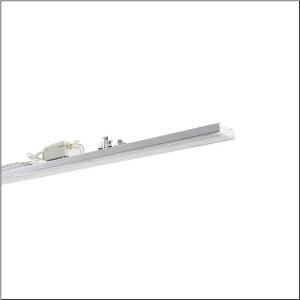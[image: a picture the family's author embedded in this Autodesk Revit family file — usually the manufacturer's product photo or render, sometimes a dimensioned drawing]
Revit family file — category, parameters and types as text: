
# Revit family: licross_r__21_recessed_mo_52tl12dn465g_46f0
name_source: partatom
category: Lighting Fixtures
units: mm (PartAtom-declared; Revit-internal decimal feet)

## family parameters
Cut with Voids When Loaded = No
Host = Face
Light Source = No
Part Type = Normal
Room Calculation Point = No
Round Connector Dimension = Use Diameter
Shared = No

## types (1)
- --- (1 x LED, 6500 lm, 35.1 W, 4000K)
    Apparent Load = 35 VA
    CIE Flux Codes = 72 92 99 100 100
    Color Rendering = 80
    Color Temperature = 4000K
    Default Elevation = 1800 mm
    Description = Licross® 21 Recessed MO, luminaire insert, of sheet steel, galvanised, coil coated, white, length: 1.500mm, width: 66mm, height: 67mm, LED rated luminous flux: 6.500lm, light colour: 840, control gear: DALI 2, with plug, 5-pole, with phase selection, mains connection: 220..240V, AC, 50/60Hz, rated input power: 35W, halogen-free wiring, primary optical cover: cover, of PMMA, light emission: direct distribution, primary light characteristic: symmetric, protection rating (complete): IP40, insulation class (complete): insulation class I (protective earthing), certification: CE, ENEC, VDE, UKCA, protection symbol: D if used in an environment without relevant dust loads with corresponding accessories, impact resistance: IK06, permissible ambient temperature for indoor applications: -25..+45°C, corresponds to IFS (International Featured Standards) requirements for safety and quality in the food industry, reducing of maximum allowable ambient temperature of 5°C with ceiling mounting, LABS conformity tested according to VDMA 24364:2018-05, packaging unit: 1 piece
    Height = 58 mm
    Lamp = 1 x LED
    Lamp Light Flux = 6500 lm
    Lamp Power = 35.1 W
    Lamp count = 1
    Length = 1500 mm
    Luminous efficacy = 185 lm/W
    Manufacturer = Siteco
    ModVariant = No
    Model = 52TL12DN465G
    Mounting Place = Ceiling
    Mounting Type = Pendant
    Number of Poles = 1
    OnlyDefault = Yes
    Power Factor = 1
    Product Name = Licross® 21 Recessed MO
    Product group = luminaire insert
    ProductGroupID = 901
    Protection Class = Protection class I
    Protection Degree = IP 40
    RLX_Detail_Level = 1
    RLX_Emergency_Light_Flux = 0 lm
    RLX_Emergency_Type = 0
    RLX_Emergency_Type_DB = No
    RlxData = <blob elided: 24209 chars, md5=dc8b457b>
    Socket = socket
    Standby Power = 0 W
    System Light Flux = 6500 lm
    System Power = 35 W
    Type Comments = factory setting: luminous flux: 100 % | dim-lin: 254 | 238 mA
    Type Image = l_1296930.jpg
    URL = http://relux.com
    VarID = @adj_057751
    Voltage = 0 V
    Weight = 0.00 kg
    Width = 66 mm

## geometry (parser evidence)
native form markers: Blend x4, Sweep x11
no freeform markers — native parametric forms only
